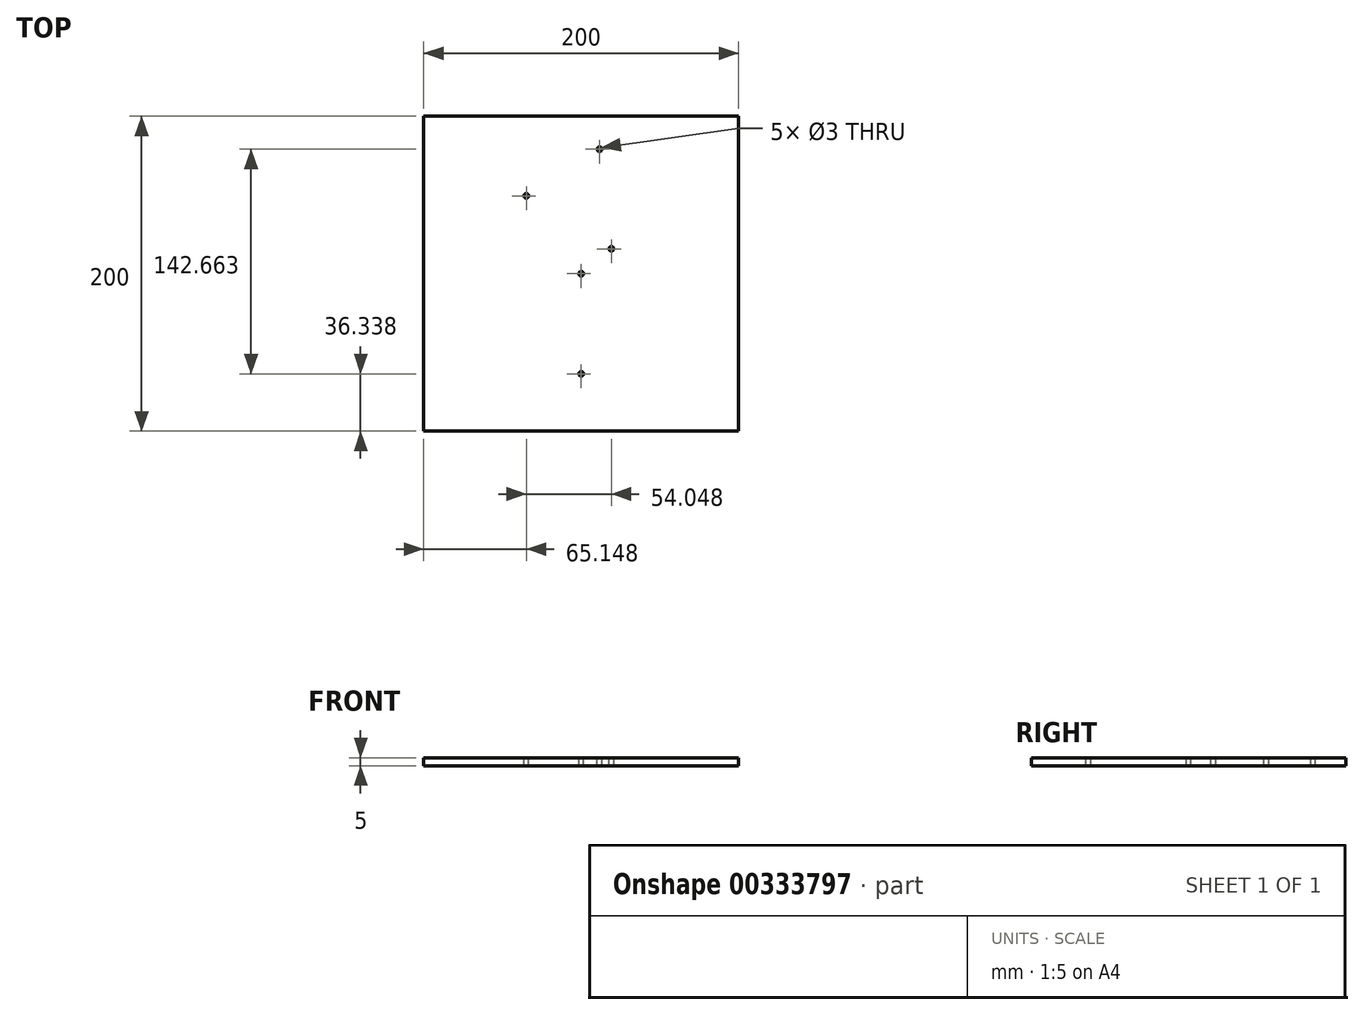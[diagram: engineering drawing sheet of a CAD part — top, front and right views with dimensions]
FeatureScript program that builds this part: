
annotation { "Feature Type Name" : "Feature", "Feature Type Description" : "" }
export const myFeature = defineFeature(function(context is Context, id is Id, definition is map)
    precondition{}
    {
        {
            var Q0;
            Q0=qCreatedBy(makeId("Top.planeOp"),FACE);
            var sketch = newSketch(context, id + "F0", { "sketchPlane" : qUnion([Q0])});
            skLineSegment(sketch, "E0.bottom", {"start": v(100, 100) * mm, "end": v(-100, 100) * mm});
            skLineSegment(sketch, "E0.top", {"start": v(100, -100) * mm, "end": v(-100, -100) * mm});
            skLineSegment(sketch, "E0.left", {"start": v(100, 100) * mm, "end": v(100, -100) * mm});
            skLineSegment(sketch, "E0.right", {"start": v(-100, 100) * mm, "end": v(-100, -100) * mm});
            skPoint(sketch, "E0.middle", {"position": v(0, 0) * mm});
            skSolve(sketch);
        }
        {
            var Q0;
            Q0=qSketchRegion(id+"F0",true);
            extrude(context, id + "F1", {"entities" : qUnion([Q0]), "depth" : 5 * mm});
        }
        {
            var Q0;
            Q0=makeQuery(id+"F1.opExtrude","CAP_FACE",FACE,{"disambiguationData":[OSD([sQuery(id+"F0.wireOp",EDGE,"E0.bottom"),sQuery(id+"F0.wireOp",EDGE,"E0.top"),sQuery(id+"F0.wireOp",EDGE,"E0.left"),sQuery(id+"F0.wireOp",EDGE,"E0.right")])],"isStart":false});
            var sketch = newSketch(context, id + "F2", { "sketchPlane" : qUnion([Q0])});
            skCircle(sketch, "E1", {"center": v(0, 0) * mm, "radius": 1.5 * mm});
            skCircle(sketch, "E2", {"center": v(0, -63.66) * mm, "radius": 1.5 * mm});
            skCircle(sketch, "E3", {"center": v(11.66, 79) * mm, "radius": 1.5 * mm});
            skCircle(sketch, "E4", {"center": v(-34.85, 49.43) * mm, "radius": 1.5 * mm});
            skCircle(sketch, "E5", {"center": v(19.2, 15.79) * mm, "radius": 1.5 * mm});
            skSolve(sketch);
        }
        {
            var Q0;
            Q0=qSketchRegion(id+"F2",true);
            extrude(context, id + "F3", {"entities" : qUnion([Q0]), "operationType" : NewBodyOperationType.REMOVE, "endBound" : BoundingType.THROUGH_ALL, "oppositeDirection" : true, "depth" : 25 * mm});
        }
    });
